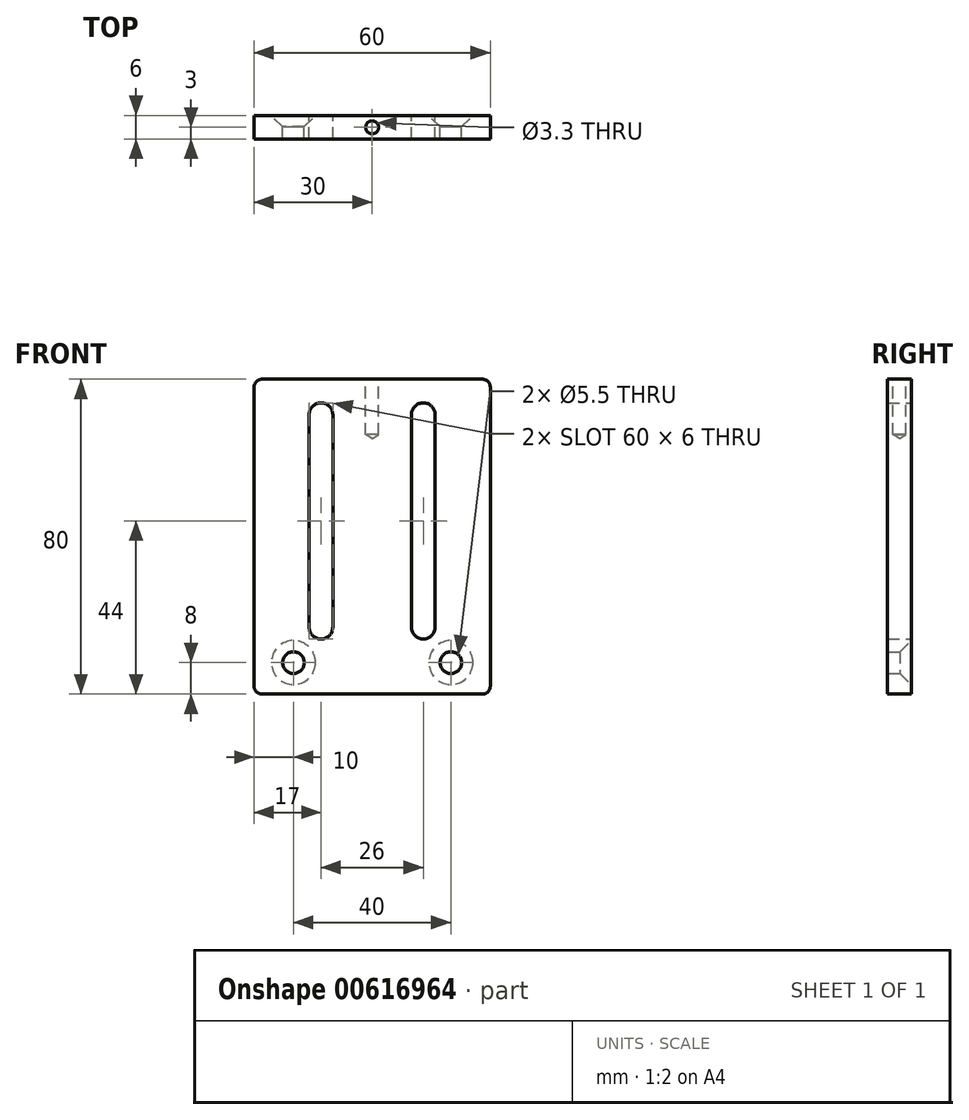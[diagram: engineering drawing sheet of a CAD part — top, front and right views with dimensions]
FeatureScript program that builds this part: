
annotation { "Feature Type Name" : "Feature", "Feature Type Description" : "" }
export const myFeature = defineFeature(function(context is Context, id is Id, definition is map)
    precondition{}
    {
        {
            var Q0;
            Q0=qCreatedBy(makeId("Front.planeOp"),FACE);
            var sketch = newSketch(context, id + "F0", { "sketchPlane" : qUnion([Q0])});
            skLineSegment(sketch, "E0.bottom", {"start": v(-28, 40) * mm, "end": v(28, 40) * mm});
            skLineSegment(sketch, "E0.top", {"start": v(-28, -40) * mm, "end": v(28, -40) * mm});
            skLineSegment(sketch, "E0.left", {"start": v(-30, 38) * mm, "end": v(-30, -38) * mm});
            skLineSegment(sketch, "E0.right", {"start": v(30, 38) * mm, "end": v(30, -38) * mm});
            skLineSegment(sketch, "E1.bottom", {"start": v(-13, 34) * mm, "end": v(-13, 34) * mm});
            skLineSegment(sketch, "E1.top", {"start": v(-13, -26) * mm, "end": v(-13, -26) * mm});
            skLineSegment(sketch, "E1.left", {"start": v(-16, 31) * mm, "end": v(-16, -23) * mm});
            skLineSegment(sketch, "E1.right", {"start": v(-10, 31) * mm, "end": v(-10, -23) * mm});
            skLineSegment(sketch, "E2.bottom", {"start": v(13, 34) * mm, "end": v(13, 34) * mm});
            skLineSegment(sketch, "E2.top", {"start": v(13, -26) * mm, "end": v(13, -26) * mm});
            skLineSegment(sketch, "E2.left", {"start": v(10, 31) * mm, "end": v(10, -23) * mm});
            skLineSegment(sketch, "E2.right", {"start": v(16, 31) * mm, "end": v(16, -23) * mm});
            skPoint(sketch, "E3.visualSharp", {"position": v(-10, -26) * mm});
            skArc(sketch, "E3.filletArc", {"start": v(-13, -26) * mm, "mid": v(-10.88, -25.12) * mm, "end": v(-10, -23) * mm});
            skPoint(sketch, "E4.visualSharp", {"position": v(-16, -26) * mm});
            skArc(sketch, "E4.filletArc", {"start": v(-16, -23) * mm, "mid": v(-15.12, -25.12) * mm, "end": v(-13, -26) * mm});
            skPoint(sketch, "E5.visualSharp", {"position": v(-16, 34) * mm});
            skArc(sketch, "E5.filletArc", {"start": v(-13, 34) * mm, "mid": v(-15.12, 33.12) * mm, "end": v(-16, 31) * mm});
            skPoint(sketch, "E6.visualSharp", {"position": v(-10, 34) * mm});
            skArc(sketch, "E6.filletArc", {"start": v(-10, 31) * mm, "mid": v(-10.88, 33.12) * mm, "end": v(-13, 34) * mm});
            skPoint(sketch, "E7.visualSharp", {"position": v(10, 34) * mm});
            skArc(sketch, "E7.filletArc", {"start": v(13, 34) * mm, "mid": v(10.88, 33.12) * mm, "end": v(10, 31) * mm});
            skPoint(sketch, "E8.visualSharp", {"position": v(16, 34) * mm});
            skArc(sketch, "E8.filletArc", {"start": v(16, 31) * mm, "mid": v(15.12, 33.12) * mm, "end": v(13, 34) * mm});
            skPoint(sketch, "E9.visualSharp", {"position": v(16, -26) * mm});
            skArc(sketch, "E9.filletArc", {"start": v(13, -26) * mm, "mid": v(15.12, -25.12) * mm, "end": v(16, -23) * mm});
            skPoint(sketch, "E10.visualSharp", {"position": v(10, -26) * mm});
            skArc(sketch, "E10.filletArc", {"start": v(10, -23) * mm, "mid": v(10.88, -25.12) * mm, "end": v(13, -26) * mm});
            skPoint(sketch, "E11", {"position": v(-20, -32) * mm});
            skPoint(sketch, "E12", {"position": v(20, -32) * mm});
            skPoint(sketch, "E13.visualSharp", {"position": v(30, 40) * mm});
            skArc(sketch, "E13.filletArc", {"start": v(30, 38) * mm, "mid": v(29.41, 39.41) * mm, "end": v(28, 40) * mm});
            skPoint(sketch, "E14.visualSharp", {"position": v(-30, 40) * mm});
            skArc(sketch, "E14.filletArc", {"start": v(-28, 40) * mm, "mid": v(-29.41, 39.41) * mm, "end": v(-30, 38) * mm});
            skPoint(sketch, "E15.visualSharp", {"position": v(30, -40) * mm});
            skArc(sketch, "E15.filletArc", {"start": v(28, -40) * mm, "mid": v(29.41, -39.41) * mm, "end": v(30, -38) * mm});
            skPoint(sketch, "E16.visualSharp", {"position": v(-30, -40) * mm});
            skArc(sketch, "E16.filletArc", {"start": v(-30, -38) * mm, "mid": v(-29.41, -39.41) * mm, "end": v(-28, -40) * mm});
            skSolve(sketch);
        }
        {
            var Q0;
            Q0=makeQuery(id+"F0.imprint","IMPRINT",FACE,{"disambiguationData":[TD([[makeQuery(id+"F0.imprint","IMPRINT",EDGE,{"derivedFrom":sQuery(id+"F0.wireOp",EDGE,"E0.bottom")}),-1.0]])]});
            extrude(context, id + "F1", {"entities" : qUnion([Q0]), "depth" : 6 * mm, "offsetDistance" : 25 * mm});
        }
        {
            var Q0;
            Q0=sQuery(id+"F0.wireOp",VERTEX,"E11");
            var Q1;
            Q1=sQuery(id+"F0.wireOp",VERTEX,"E12");
            var Q2;
            Q2=makeQuery(id+"F1.opExtrude","SWEPT_BODY",BODY,{"disambiguationData":[OSD([sQuery(id+"F0.wireOp",EDGE,"E0.bottom"),sQuery(id+"F0.wireOp",EDGE,"E0.top"),sQuery(id+"F0.wireOp",EDGE,"E0.left"),sQuery(id+"F0.wireOp",EDGE,"E0.right"),sQuery(id+"F0.wireOp",EDGE,"E1.left"),sQuery(id+"F0.wireOp",EDGE,"E1.right"),sQuery(id+"F0.wireOp",EDGE,"E2.left"),sQuery(id+"F0.wireOp",EDGE,"E2.right"),sQuery(id+"F0.wireOp",EDGE,"E3.filletArc"),sQuery(id+"F0.wireOp",EDGE,"E4.filletArc"),sQuery(id+"F0.wireOp",EDGE,"E5.filletArc"),sQuery(id+"F0.wireOp",EDGE,"E6.filletArc"),sQuery(id+"F0.wireOp",EDGE,"E7.filletArc"),sQuery(id+"F0.wireOp",EDGE,"E8.filletArc"),sQuery(id+"F0.wireOp",EDGE,"E9.filletArc"),sQuery(id+"F0.wireOp",EDGE,"E10.filletArc")])]});
            hole(context, id + "F2", {"style" : HoleStyle.C_SINK, "endStyle" : HoleEndStyle.BLIND, "oppositeDirection" : true, "standardTappedOrClearance" : lookupTablePath({ "standard" : "ISO", "fit" : "Normal", "size" : "M5", "type" : "Clearance" }), "standardBlindInLast" : lookupTablePath({ "fit" : "Standard", "standard" : "ISO", "size" : "M5", "type" : "Clearance" }), "holeDiameter" : 5.5 * mm, "cSinkDiameter" : 11.2 * mm, "cSinkAngle" : 90 * degree, "majorDiameter" : 5 * mm, "holeDepth" : 19 * mm, "isTappedThrough" : true, "tappedDepth" : 16.6 * mm, "tapClearance" : 3, "locations" : qUnion([Q0, Q1]), "scope" : qUnion([Q2])});
        }
        {
            var Q0;
            Q0=makeQuery(id+"F1.opExtrude","SWEPT_FACE",FACE,{"disambiguationData":[OSD([sQuery(id+"F0.wireOp",EDGE,"E0.bottom")])]});
            var sketch = newSketch(context, id + "F3", { "sketchPlane" : qUnion([Q0])});
            skPoint(sketch, "E17", {"position": v(0, -3) * mm});
            skSolve(sketch);
        }
        {
            var Q0;
            Q0=sQuery(id+"F3.wireOp",VERTEX,"E17");
            var Q1;
            Q1=makeQuery(id+"F1.opExtrude","SWEPT_BODY",BODY,{"disambiguationData":[OSD([sQuery(id+"F0.wireOp",EDGE,"E0.bottom"),sQuery(id+"F0.wireOp",EDGE,"E0.top"),sQuery(id+"F0.wireOp",EDGE,"E0.left"),sQuery(id+"F0.wireOp",EDGE,"E0.right"),sQuery(id+"F0.wireOp",EDGE,"E1.left"),sQuery(id+"F0.wireOp",EDGE,"E1.right"),sQuery(id+"F0.wireOp",EDGE,"E2.left"),sQuery(id+"F0.wireOp",EDGE,"E2.right"),sQuery(id+"F0.wireOp",EDGE,"E3.filletArc"),sQuery(id+"F0.wireOp",EDGE,"E4.filletArc"),sQuery(id+"F0.wireOp",EDGE,"E5.filletArc"),sQuery(id+"F0.wireOp",EDGE,"E6.filletArc"),sQuery(id+"F0.wireOp",EDGE,"E7.filletArc"),sQuery(id+"F0.wireOp",EDGE,"E8.filletArc"),sQuery(id+"F0.wireOp",EDGE,"E9.filletArc"),sQuery(id+"F0.wireOp",EDGE,"E10.filletArc"),sQuery(id+"F0.wireOp",EDGE,"E13.filletArc"),sQuery(id+"F0.wireOp",EDGE,"E14.filletArc"),sQuery(id+"F0.wireOp",EDGE,"E15.filletArc"),sQuery(id+"F0.wireOp",EDGE,"E16.filletArc")])]});
            hole(context, id + "F4", {"style" : HoleStyle.SIMPLE, "endStyle" : HoleEndStyle.BLIND, "standardTappedOrClearance" : lookupTablePath({ "standard" : "ISO", "engagement" : "75%", "pitch" : "0.7 mm", "size" : "M4", "type" : "Tapped" }), "standardBlindInLast" : lookupTablePath({ "standard" : "ISO", "engagement" : "75%", "pitch" : "0.7 mm", "size" : "M4", "type" : "Tapped" }), "holeDiameter" : 3.3 * mm, "majorDiameter" : 4 * mm, "showTappedDepth" : true, "holeDepth" : 14.1 * mm, "isTappedThrough" : true, "tappedDepth" : 12 * mm, "tapClearance" : 3, "locations" : qUnion([Q0]), "scope" : qUnion([Q1])});
        }
    });
